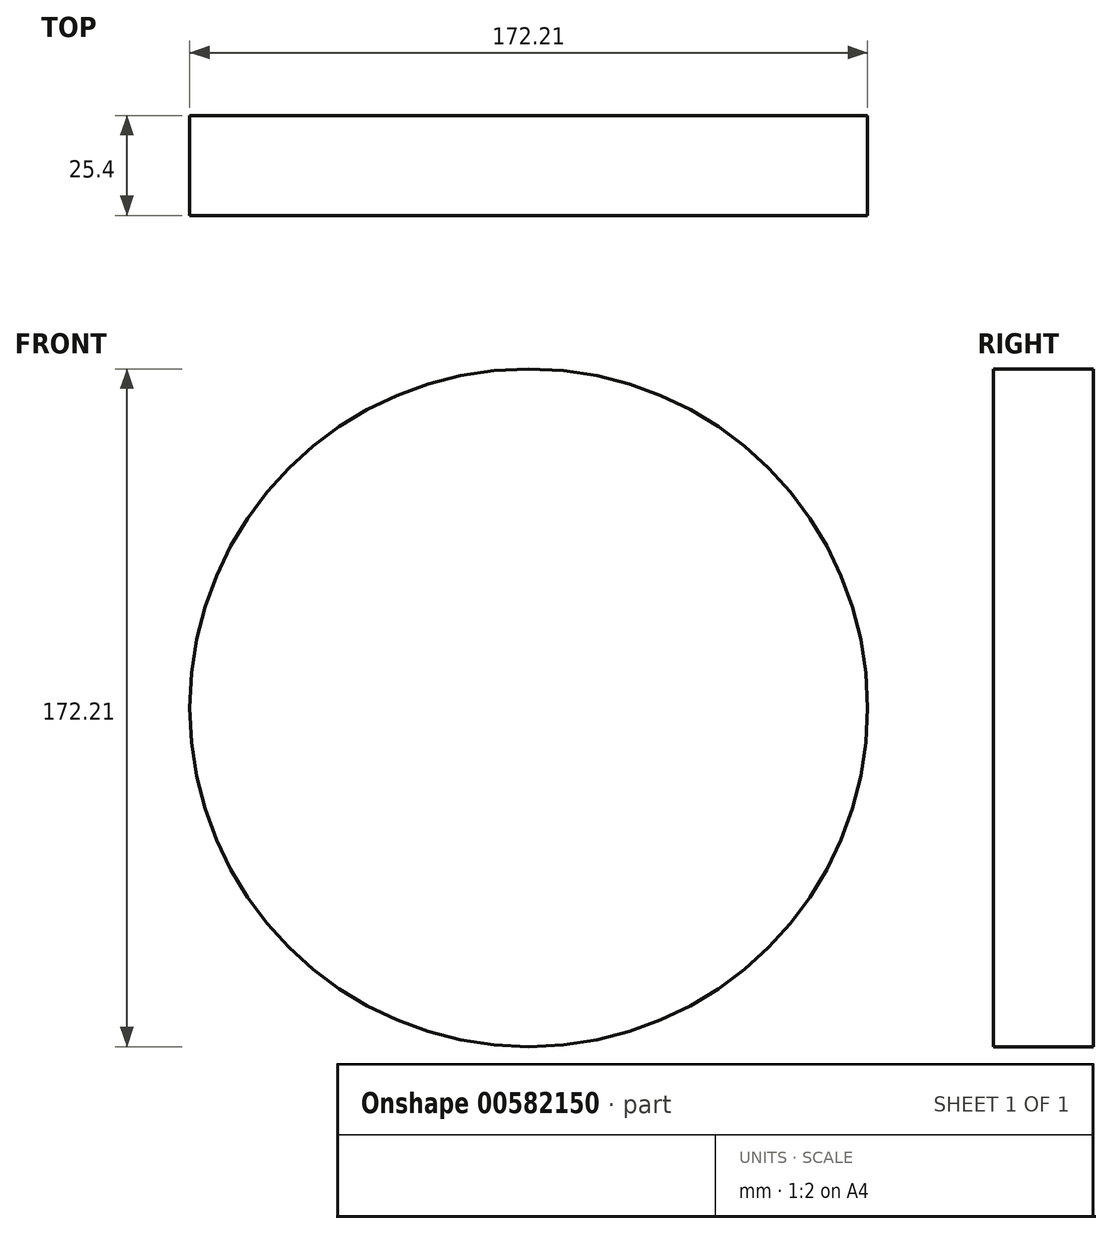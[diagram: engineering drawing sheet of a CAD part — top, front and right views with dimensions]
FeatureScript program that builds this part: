
annotation { "Feature Type Name" : "Feature", "Feature Type Description" : "" }
export const myFeature = defineFeature(function(context is Context, id is Id, definition is map)
    precondition{}
    {
        {
            var Q0;
            Q0=qCreatedBy(makeId("Front.planeOp"),FACE);
            var sketch = newSketch(context, id + "F0", { "sketchPlane" : qUnion([Q0])});
            skCircle(sketch, "E0", {"center": v(9.51, -16.14) * mm, "radius": 86.1 * mm});
            skCircle(sketch, "E1", {"center": v(31.46, 28.45) * mm, "radius": 49.12 * mm, "construction": true});
            skCircle(sketch, "E2", {"center": v(77.13, -29.35) * mm, "radius": 2.07 * mm, "construction": true});
            skSolve(sketch);
        }
        {
            var Q0;
            Q0=makeQuery(id+"F0.imprint","IMPRINT",FACE,{"disambiguationData":[TD([[makeQuery(id+"F0.imprint","IMPRINT",EDGE,{"derivedFrom":sQuery(id+"F0.wireOp",EDGE,"E0")}),1.0]])]});
            extrude(context, id + "F1", {"entities" : qUnion([Q0]), "depth" : 25.4 * mm, "offsetDistance" : 25.4 * mm});
        }
    });
